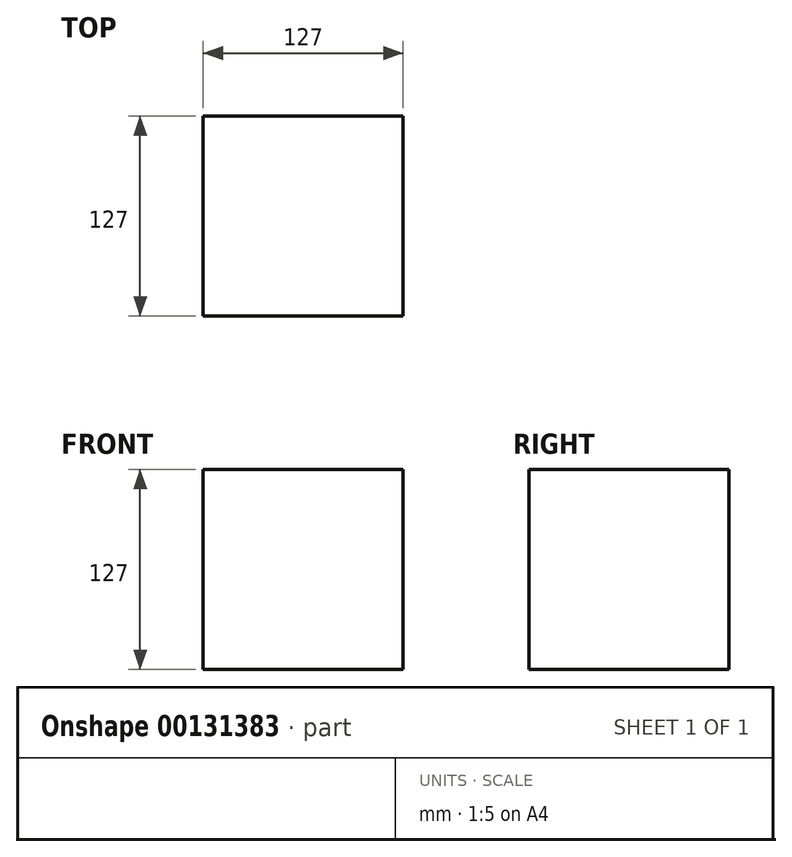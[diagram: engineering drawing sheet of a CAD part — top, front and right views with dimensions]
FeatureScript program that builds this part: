
annotation { "Feature Type Name" : "Feature", "Feature Type Description" : "" }
export const myFeature = defineFeature(function(context is Context, id is Id, definition is map)
    precondition{}
    {
        {
            var Q0;
            Q0=qCreatedBy(makeId("Front.planeOp"),FACE);
            var sketch = newSketch(context, id + "F0", { "sketchPlane" : qUnion([Q0])});
            skLineSegment(sketch, "E0.bottom", {"start": v(-119.62, 127) * mm, "end": v(7.38, 127) * mm});
            skLineSegment(sketch, "E0.top", {"start": v(-119.62, 0) * mm, "end": v(7.38, 0) * mm});
            skLineSegment(sketch, "E0.left", {"start": v(-119.62, 127) * mm, "end": v(-119.62, 0) * mm});
            skLineSegment(sketch, "E0.right", {"start": v(7.38, 127) * mm, "end": v(7.38, 0) * mm});
            skSolve(sketch);
        }
        {
            var Q0;
            Q0=makeQuery(id+"F0.imprint","IMPRINT",FACE,{"disambiguationData":[TD([[makeQuery(id+"F0.imprint","IMPRINT",EDGE,{"derivedFrom":sQuery(id+"F0.wireOp",EDGE,"E0.bottom")}),-1.0]])]});
            extrude(context, id + "F1", {"entities" : qUnion([Q0]), "depth" : 127 * mm});
        }
    });
